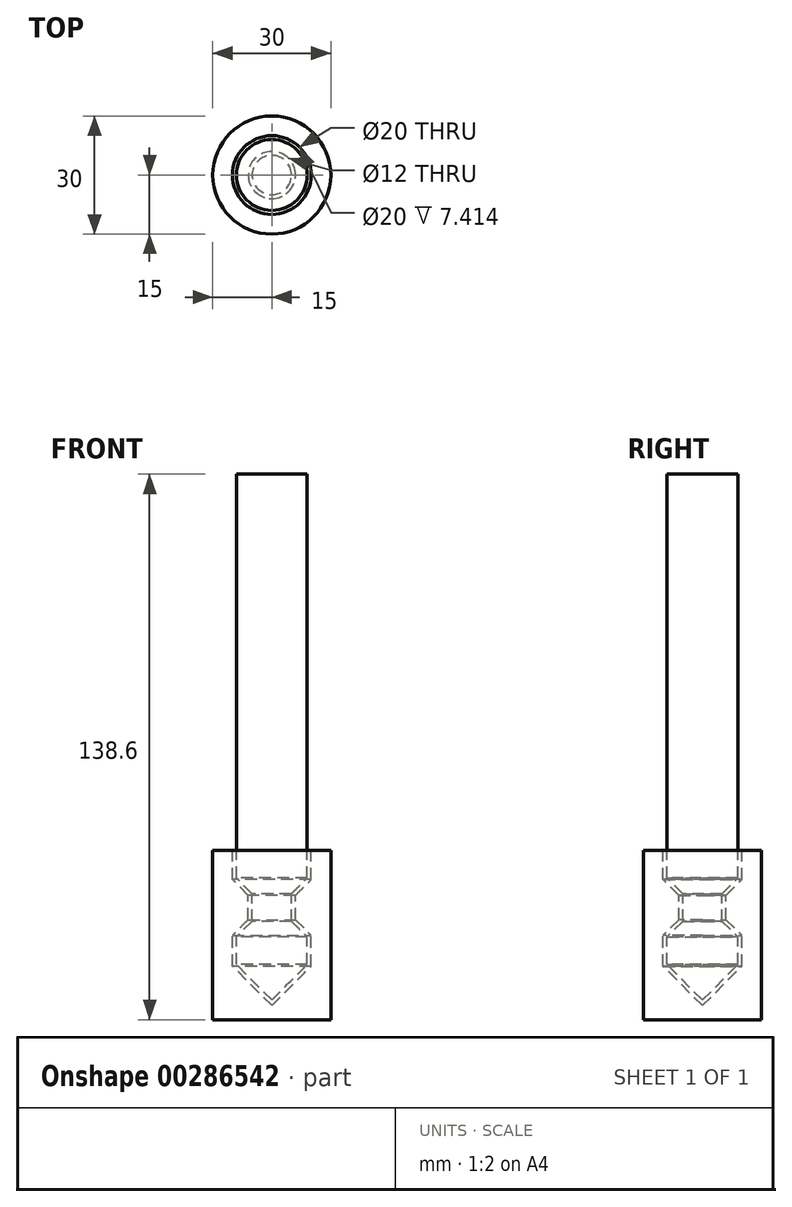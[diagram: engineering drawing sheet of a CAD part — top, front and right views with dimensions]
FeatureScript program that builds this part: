
annotation { "Feature Type Name" : "Feature", "Feature Type Description" : "" }
export const myFeature = defineFeature(function(context is Context, id is Id, definition is map)
    precondition{}
    {
        {
            assignVariable(context, id + "F0", {"name" : "tSpace", "anyValue" : 1});
        }
        {
            var Q0;
            Q0=qCreatedBy(makeId("Top.planeOp"),FACE);
            var sketch = newSketch(context, id + "F1", { "sketchPlane" : qUnion([Q0])});
            skCircle(sketch, "E0", {"center": v(0, 0) * mm, "radius": 15 * mm});
            skSolve(sketch);
        }
        {
            var Q0;
            Q0 = qSketchRegion(id + "F1", true);
            extrude(context, id + "F2", {"entities" : qUnion([Q0]), "depth" : 43 * mm});
        }
        {
            var Q0;
            Q0=qCreatedBy(makeId("Front.planeOp"),FACE);
            var sketch = newSketch(context, id + "F3", { "sketchPlane" : qUnion([Q0])});
            skLineSegment(sketch, "E1", {"start": v(0, 5) * mm, "end": v(9, 14) * mm});
            skLineSegment(sketch, "E2", {"start": v(9, 14) * mm, "end": v(9, 21) * mm});
            skLineSegment(sketch, "E3", {"start": v(9, 21) * mm, "end": v(5, 25) * mm});
            skLineSegment(sketch, "E4", {"start": v(5, 25) * mm, "end": v(5, 32) * mm});
            skLineSegment(sketch, "E5", {"start": v(5, 138.6) * mm, "end": v(0, 138.6) * mm});
            skLineSegment(sketch, "E6", {"start": v(0, 138.6) * mm, "end": v(0, 5) * mm});
            skLineSegment(sketch, "E7", {"start": v(5, 32) * mm, "end": v(9, 36) * mm});
            skLineSegment(sketch, "E8", {"start": v(9, 36) * mm, "end": v(9, 138.6) * mm});
            skLineSegment(sketch, "E9", {"start": v(9, 138.6) * mm, "end": v(5, 138.6) * mm});
            skSolve(sketch);
        }
        {
            var Q0;
            Q0 = qSketchRegion(id + "F3", true);
            var Q1;
            Q1=sQuery(id+"F3.wireOp",EDGE,"E6");
            revolve(context, id + "F4", {"entities" : qUnion([Q0]), "axis" : qUnion([Q1]), "revolveType" : RevolveType.FULL});
        }
        {
            var Q0;
            Q0=makeQuery(id+"F4.opRevolve","SWEPT_BODY",BODY,{"disambiguationData":[OSD([sQuery(id+"F3.wireOp",EDGE,"E1"),sQuery(id+"F3.wireOp",EDGE,"E2"),sQuery(id+"F3.wireOp",EDGE,"E3"),sQuery(id+"F3.wireOp",EDGE,"E4"),sQuery(id+"F3.wireOp",EDGE,"E5"),sQuery(id+"F3.wireOp",EDGE,"E6"),sQuery(id+"F3.wireOp",EDGE,"E7"),sQuery(id+"F3.wireOp",EDGE,"E8"),sQuery(id+"F3.wireOp",EDGE,"E9")])]});
            var Q1;
            Q1=makeQuery(id+"F2.opExtrude","SWEPT_BODY",BODY,{"disambiguationData":[OSD([sQuery(id+"F1.wireOp",EDGE,"E0")])]});
            booleanBodies(context, id + "F5", {"operationType" : BooleanOperationType.SUBTRACTION, "tools" : qUnion([Q0]), "targets" : qUnion([Q1]), "offset" : true, "offsetAll" : true, "offsetDistance" : (getVariable(context, 'tSpace')) * mm, "keepTools" : true});
        }
    });
